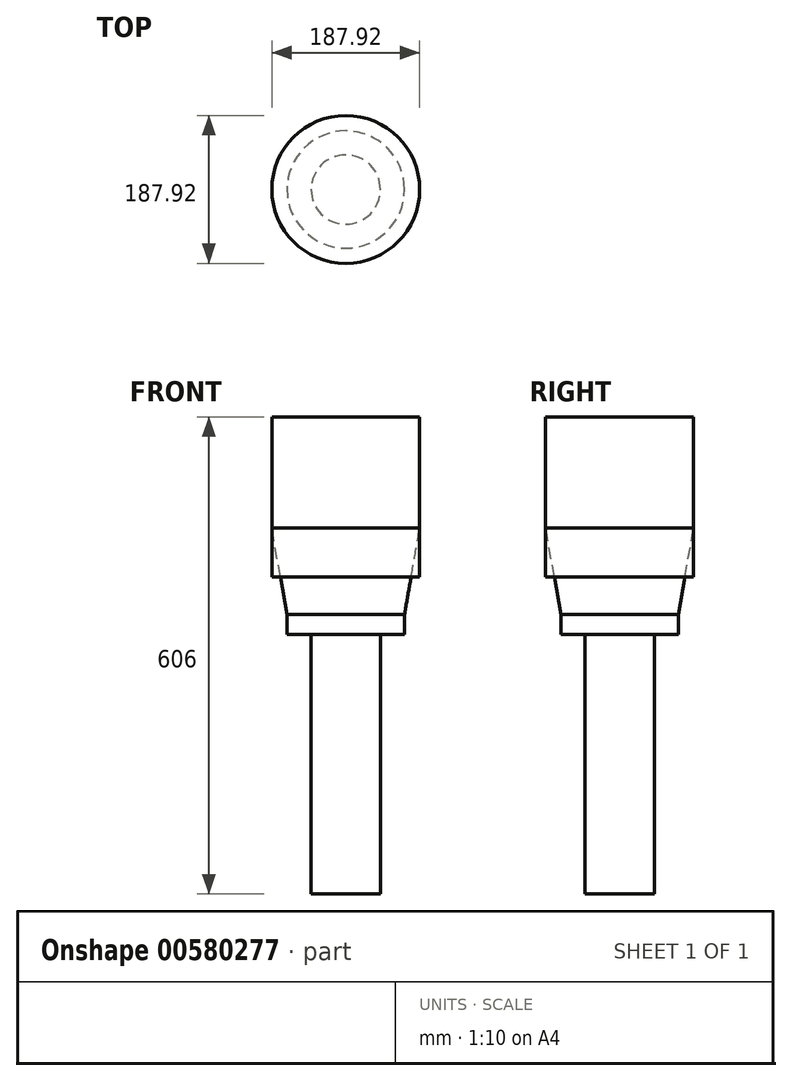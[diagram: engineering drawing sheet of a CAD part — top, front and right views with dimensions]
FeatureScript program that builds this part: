
annotation { "Feature Type Name" : "Feature", "Feature Type Description" : "" }
export const myFeature = defineFeature(function(context is Context, id is Id, definition is map)
    precondition{}
    {
        {
            var Q0;
            Q0=qCreatedBy(makeId("Top.planeOp"),FACE);
            var sketch = newSketch(context, id + "F0", { "sketchPlane" : qUnion([Q0])});
            skCircle(sketch, "E0", {"center": v(0, 0) * mm, "radius": 74.56 * mm});
            skSolve(sketch);
        }
        {
            var Q0;
            Q0 = qSketchRegion(id + "F0", true);
            extrude(context, id + "F1", {"entities" : qUnion([Q0]), "depth" : 25 * mm, "offsetDistance" : 25 * mm});
        }
        {
            var Q0;
            Q0=makeQuery(id+"F1.opExtrude","CAP_FACE",FACE,{"disambiguationData":[OSD([sQuery(id+"F0.wireOp",EDGE,"E0")])],"isStart":false});
            extrude(context, id + "F2", {"entities" : qUnion([Q0]), "operationType" : NewBodyOperationType.ADD, "depth" : 110 * mm, "offsetDistance" : 25 * mm, "hasDraft" : true, "draftAngle" : 10 * degree});
        }
        {
            var Q0;
            Q0=qCreatedBy(makeId("Top.planeOp"),FACE);
            var sketch = newSketch(context, id + "F3", { "sketchPlane" : qUnion([Q0])});
            skCircle(sketch, "E1", {"center": v(0, 0) * mm, "radius": 57.26 * mm});
            skSolve(sketch);
        }
        {
            var Q0;
            Q0 = qSketchRegion(id + "F3", true);
            var Q1;
            Q1=makeQuery(id+"F2.opExtrude","CAP_FACE",FACE,{"disambiguationData":[OSD([sQuery(id+"F0.wireOp",EDGE,"E0")])],"isStart":false});
            extrude(context, id + "F4", {"entities" : qUnion([Q0, Q1]), "operationType" : NewBodyOperationType.ADD, "depth" : 141 * mm, "offsetDistance" : 25 * mm});
        }
        {
            var Q0;
            Q0=qCreatedBy(makeId("Top.planeOp"),FACE);
            var sketch = newSketch(context, id + "F5", { "sketchPlane" : qUnion([Q0])});
            skCircle(sketch, "E2", {"center": v(0, 0) * mm, "radius": 44.01 * mm});
            skSolve(sketch);
        }
        {
            var Q0;
            Q0 = qSketchRegion(id + "F5", true);
            extrude(context, id + "F6", {"entities" : qUnion([Q0]), "operationType" : NewBodyOperationType.ADD, "oppositeDirection" : true, "depth" : 330 * mm, "offsetDistance" : 25 * mm});
        }
        {
            var Q0;
            Q0 = qSketchRegion(id + "F2TAYeLJrsPooc4_1", true);
            var Q1;
            Q1=makeQuery(id+"F4.opExtrude","CAP_FACE",FACE,{"disambiguationData":[OSD([sQuery(id+"F0.wireOp",EDGE,"E0")])],"isStart":false});
            extrude(context, id + "F7", {"entities" : qUnion([Q0, Q1]), "oppositeDirection" : true, "depth" : 203 * mm, "offsetDistance" : 25 * mm});
        }
    });
